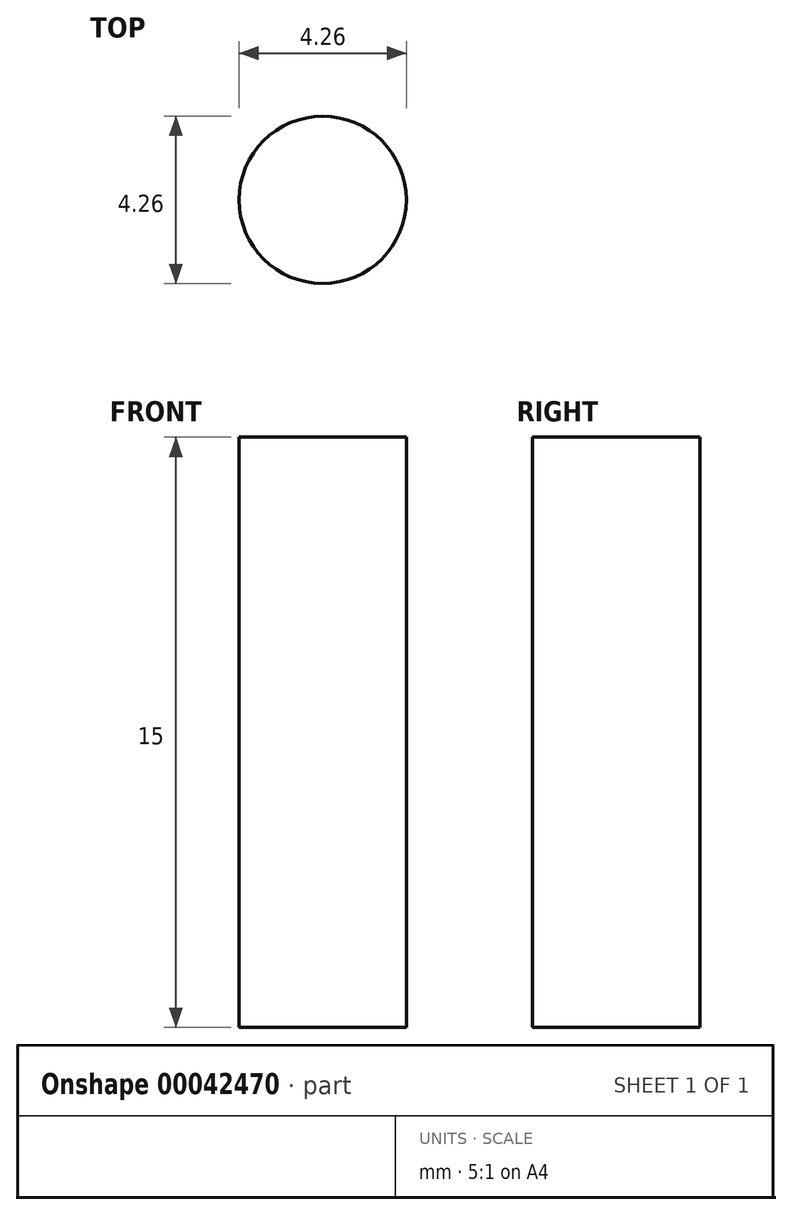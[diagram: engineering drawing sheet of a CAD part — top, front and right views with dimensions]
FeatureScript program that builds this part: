
annotation { "Feature Type Name" : "Feature", "Feature Type Description" : "" }
export const myFeature = defineFeature(function(context is Context, id is Id, definition is map)
    precondition{}
    {
        {
            var Q0;
            Q0=qCreatedBy(makeId("Top.planeOp"),FACE);
            var sketch = newSketch(context, id + "F0", { "sketchPlane" : qUnion([Q0])});
            skCircle(sketch, "E0", {"center": v(0, 0) * mm, "radius": 2.12 * mm});
            skSolve(sketch);
        }
        {
            var Q0;
            Q0 = qSketchRegion(id + "F0", true);
            extrude(context, id + "F1", {"entities" : qUnion([Q0]), "depth" : 15 * mm});
        }
    });
